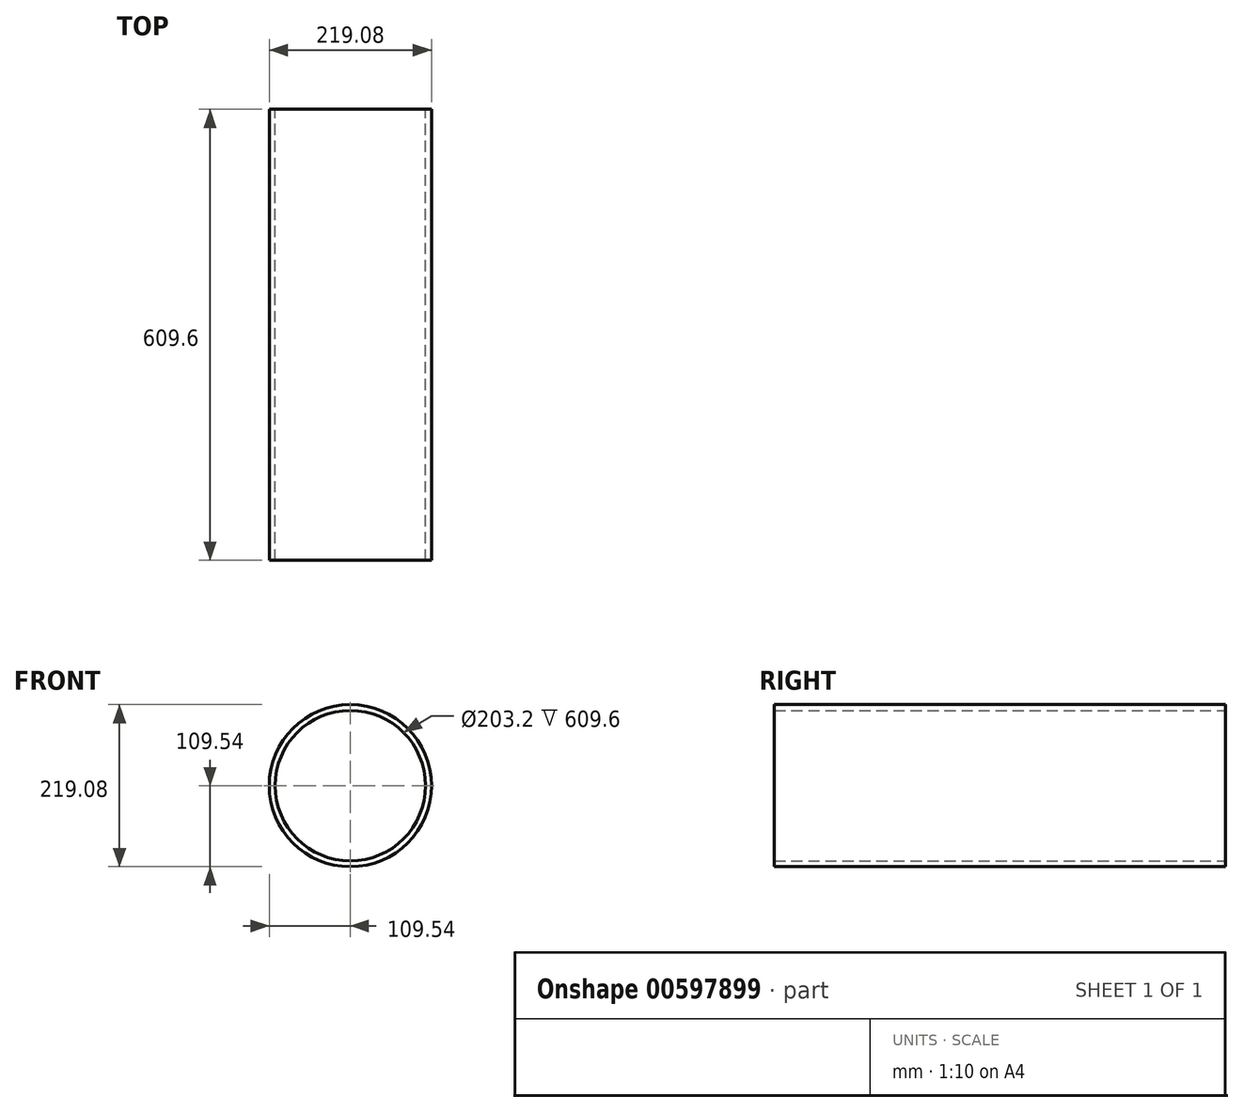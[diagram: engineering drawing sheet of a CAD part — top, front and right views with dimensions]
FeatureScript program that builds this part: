
annotation { "Feature Type Name" : "Feature", "Feature Type Description" : "" }
export const myFeature = defineFeature(function(context is Context, id is Id, definition is map)
    precondition{}
    {
        {
            var Q0;
            Q0=qCreatedBy(makeId("Front.planeOp"),FACE);
            var sketch = newSketch(context, id + "F0", { "sketchPlane" : qUnion([Q0])});
            skCircle(sketch, "E0", {"center": v(0, 0) * mm, "radius": 109.54 * mm});
            skCircle(sketch, "E1", {"center": v(0, 0) * mm, "radius": 101.6 * mm});
            skSolve(sketch);
        }
        {
            var Q0;
            Q0 = qSketchRegion(id + "F0", true);
            extrude(context, id + "F1", {"entities" : qUnion([Q0]), "depth" : 609.6 * mm, "offsetDistance" : 25.4 * mm});
        }
    });
